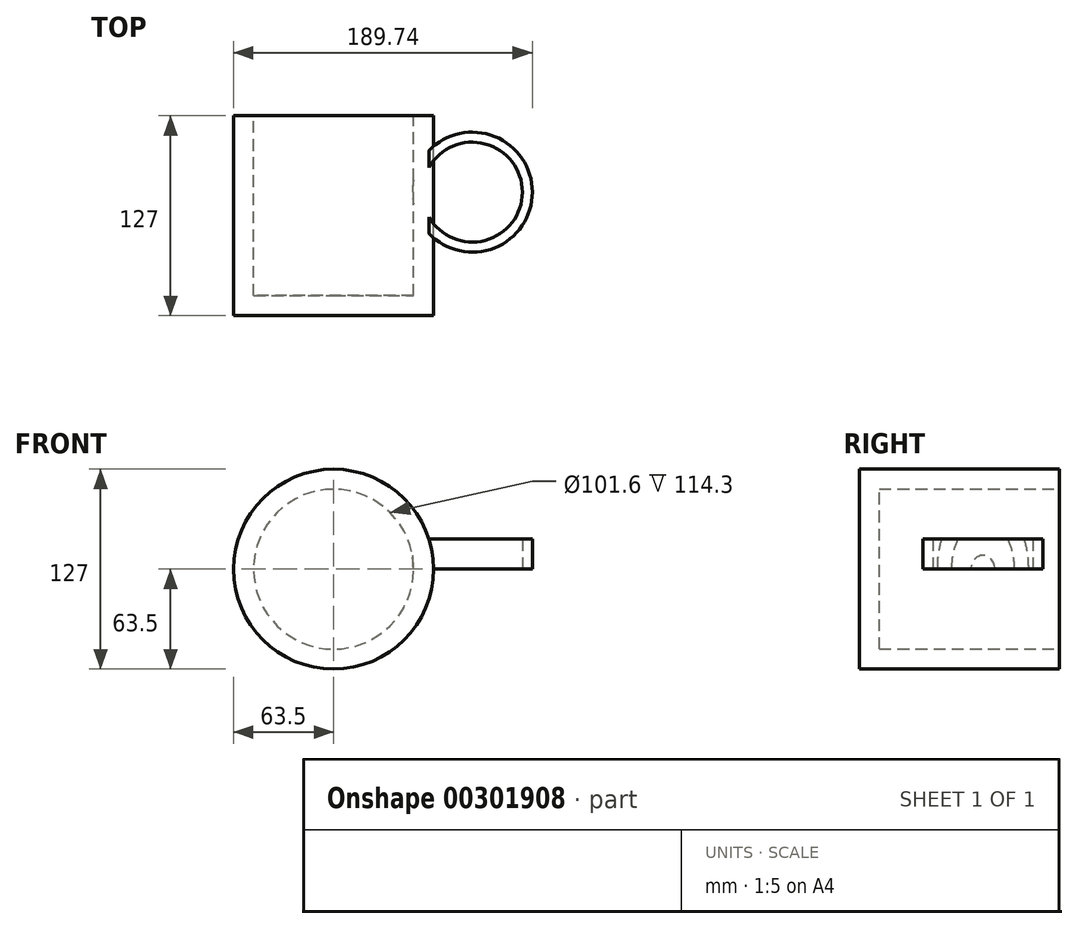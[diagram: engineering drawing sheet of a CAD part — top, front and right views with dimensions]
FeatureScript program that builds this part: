
annotation { "Feature Type Name" : "Feature", "Feature Type Description" : "" }
export const myFeature = defineFeature(function(context is Context, id is Id, definition is map)
    precondition{}
    {
        {
            var Q0;
            Q0=qCreatedBy(makeId("Front.planeOp"),FACE);
            var sketch = newSketch(context, id + "F0", { "sketchPlane" : qUnion([Q0])});
            skCircle(sketch, "E0", {"center": v(0, 0) * mm, "radius": 63.5 * mm});
            skSolve(sketch);
        }
        {
            var Q0;
            Q0=makeQuery(id+"F0.imprint","IMPRINT",FACE,{"disambiguationData":[TD([[makeQuery(id+"F0.imprint","IMPRINT",EDGE,{"derivedFrom":sQuery(id+"F0.wireOp",EDGE,"E0")}),1.0]])]});
            extrude(context, id + "F1", {"entities" : qUnion([Q0]), "depth" : 127 * mm});
        }
        {
            var Q0;
            Q0=qCreatedBy(makeId("Front.planeOp"),FACE);
            var sketch = newSketch(context, id + "F2", { "sketchPlane" : qUnion([Q0])});
            skCircle(sketch, "E1", {"center": v(0, 0) * mm, "radius": 50.8 * mm});
            skSolve(sketch);
        }
        {
            var Q0;
            Q0 = qSketchRegion(id + "F2", true);
            extrude(context, id + "F3", {"entities" : qUnion([Q0]), "operationType" : NewBodyOperationType.REMOVE, "depth" : 114.3 * mm});
        }
        {
            var Q0;
            Q0=qCreatedBy(makeId("Right.planeOp"),FACE);
            var Q1;
            Q1 = qBodyType(qCreatedBy(id + "F5" ,EDGE), BodyType.WIRE);
            cPlane(context, id + "F4", {"entities" : qUnion([Q0, Q1]), "cplaneType" : CPlaneType.OFFSET, "offset" : 63.5 * mm, "width" : 152.4 * mm, "height" : 152.4 * mm});
        }
        {
            var Q0;
            Q0=qCreatedBy(id+"F4.planeOp",FACE);
            var sketch = newSketch(context, id + "F5", { "sketchPlane" : qUnion([Q0])});
            skSolve(sketch);
        }
        {
            var Q0;
            Q0=qCreatedBy(makeId("Top.planeOp"),FACE);
            var sketch = newSketch(context, id + "F6", { "sketchPlane" : qUnion([Q0])});
            skCircle(sketch, "E2", {"center": v(88.14, -48.52) * mm, "radius": 38.1 * mm});
            skCircle(sketch, "E3", {"center": v(88.14, -48.52) * mm, "radius": 31.75 * mm});
            skSolve(sketch);
        }
        {
            var Q0;
            Q0=makeQuery(id+"F6.imprint","IMPRINT",FACE,{"disambiguationData":[TD([[makeQuery(id+"F6.imprint","IMPRINT",EDGE,{"derivedFrom":sQuery(id+"F6.wireOp",EDGE,"E2")}),1.0]])]});
            extrude(context, id + "F7", {"entities" : qUnion([Q0]), "operationType" : NewBodyOperationType.ADD, "depth" : 19.05 * mm});
        }
    });
